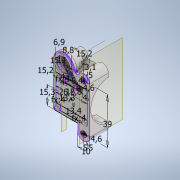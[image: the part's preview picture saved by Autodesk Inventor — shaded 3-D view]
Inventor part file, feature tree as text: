
AUTODESK INVENTOR PART (.ipt)
format: ipt  version: 2020.2 (Build 242310000, 310)  size: 471,552 bytes
history: native  units: mm
features: sketch x9, extrude x8, fillet x4, plane x2, revolve x2, projected_geometry x2, other x1
ambient origin geometry x8: Origin, YZ Plane, XZ Plane, XY Plane, X Axis, Y Axis, Z Axis, Center Point
bodies: Volumenkörper1 (feature_tree)
feature tree (28):
  extrude  "Extrusion1"  Depth=4.0mm
  sketch  "Skizze2"  dims[d4=4.0mm d6=4.0mm]
  other  "Arbeitsachse1"
  extrude  "Extrusion2"  Depth=4.0mm
  extrude  "Extrusion3"  Depth=4.0mm
  plane  "Arbeitsebene1"
  plane  "Arbeitsebene2"
  revolve  "Umdrehung1"
  sketch  "Skizze4"  dims[d9=15.4mm d10=0.8mm d11=0.0mm]
  extrude  "Extrusion4"  Depth=0.8mm TaperAngle=0.0deg
  extrude  "Extrusion5"  Depth=13.4mm
  revolve  "Umdrehung2"
  extrude  "Extrusion6"  Depth=26.6mm
  fillet  "Rundung1"  Radius=5.4mm
  fillet  "Rundung2"  Radius=4.6mm
  sketch  "Skizze8"  dims[d20=5.0mm d21=8.8mm d22=15.2mm d23=15.3mm]
  extrude  "Extrusion7"  Depth=5.0mm
  extrude  "Extrusion8"  Depth=8.8mm
  fillet  "Rundung3"  Radius=15.2mm
  fillet  "Rundung4"  Radius=15.3mm
  sketch  "Skizze1"  dims[d2=12.0mm d3=4.0mm]
  sketch  "Skizze3"  dims[d7=4.0mm d8=4.0mm]
  sketch  "Skizze5"  dims[d12=12.8mm d13=13.4mm]
  projected_geometry  "Projizierte Kontur1"
  sketch  "Skizze6"  dims[d14=13.3mm d15=26.6mm d16=5.4mm d17=4.6mm]
  projected_geometry  "Projizierte Kontur2"
  sketch  "Skizze7"  dims[d18=4.6mm d19=5.0mm]
  sketch  "Skizze9"  dims[d24=3.1mm d25=6.9mm d26=12.0mm d27=4.0mm d28=4.0mm d29=4.0mm d31=4.0mm d32=4.0mm d33=15.4mm d34=12.8mm d35=13.4mm d36=13.3mm d37=26.6mm d38=5.4mm d39=4.6mm d40=4.6mm d41=5.0mm d42=5.0mm d43=8.8mm d44=15.2mm d45=15.3mm d46=3.1mm d47=6.9mm d48=0.6mm d49=0.0mm d50=2.0mm d51=0.0mm d52=5.0mm d53=8.0mm d54=2.6mm d55=2.0mm d56=90.0deg d57=32.0mm d58=16.0mm d59=4.0mm d60=4.0mm d61=13.5mm d62=0.0mm d63=67.0mm d64=0.0mm d65=13.962634mm d66=4.0mm d67=7.31mm d68=0.0mm d69=0.0mm d70=2.0mm d71=2.0mm d72=4.5mm d73=0.0mm d74=24.5mm d76=15.75mm d77=0.0mm d78=15.75mm d79=2.0mm d80=5.4mm d81=37.0mm d82=5.0mm d83=30.4mm d85=39.0mm d86=15.2mm d87=10.0mm d88=5.0mm d89=49.0mm d90=2.0mm d91=1.0mm d75=0.872665mm]
